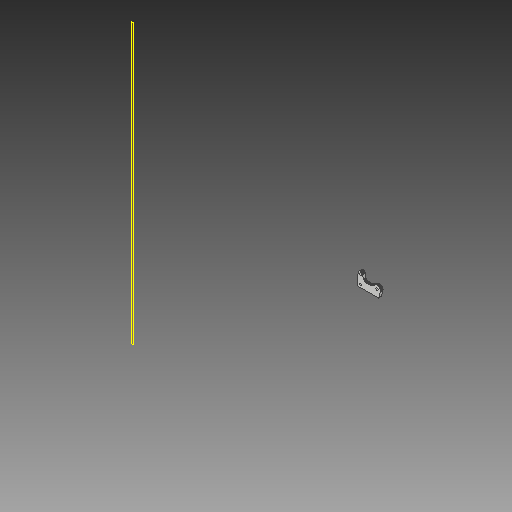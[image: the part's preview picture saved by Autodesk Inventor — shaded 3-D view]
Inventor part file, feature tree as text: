
AUTODESK INVENTOR PART (.ipt)
format: ipt  version: 2018 (Build 220112000, 112)  size: 321,536 bytes
history: native  units: mm
features: other x3, sketch x2, plane x1
ambient origin geometry x8: Origin, YZ Plane, XZ Plane, XY Plane, X Axis, Y Axis, Z Axis, Center Point
bodies: Solid1 (feature_tree)
feature tree (6):
  other  "X-Idler_MIR.ipt"
  other  "Solid1::X-Idler_MIR.ipt"
  other  "TaggingFeature1"
  sketch  "Sketch1"  dims[d0=10.0mm]
  sketch  "Sketch2"
  plane  "Work Plane1"
